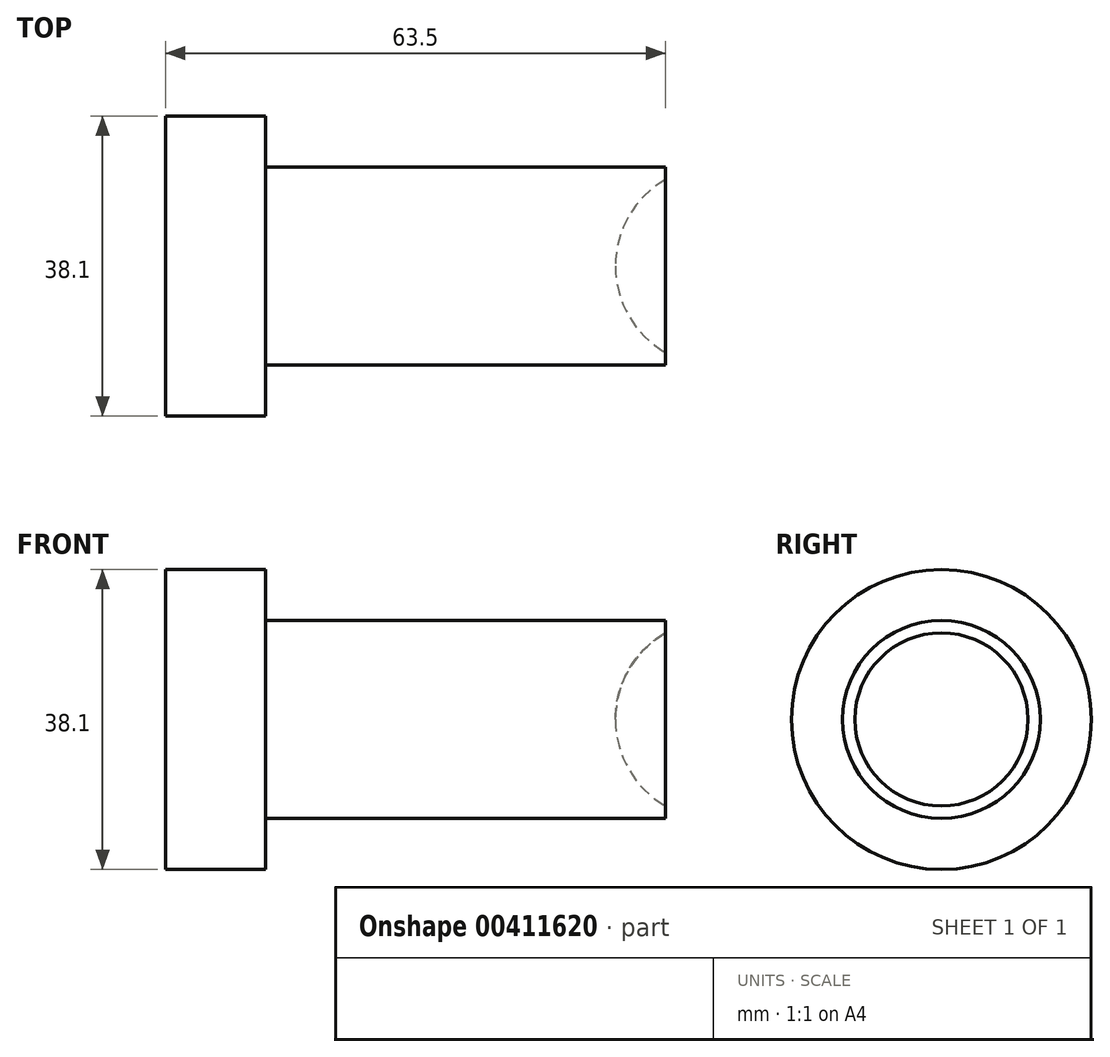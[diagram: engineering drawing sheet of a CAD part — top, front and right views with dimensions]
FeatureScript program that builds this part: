
annotation { "Feature Type Name" : "Feature", "Feature Type Description" : "" }
export const myFeature = defineFeature(function(context is Context, id is Id, definition is map)
    precondition{}
    {
        {
            var Q0;
            Q0=qCreatedBy(makeId("Right.planeOp"),FACE);
            var sketch = newSketch(context, id + "F0", { "sketchPlane" : qUnion([Q0])});
            skCircle(sketch, "E0", {"center": v(0, 0) * mm, "radius": 19.05 * mm});
            skSolve(sketch);
        }
        {
            var Q0;
            Q0 = qSketchRegion(id + "F0", true);
            extrude(context, id + "F1", {"entities" : qUnion([Q0]), "depth" : 12.7 * mm});
        }
        {
            var Q0;
            Q0=makeQuery(id+"F1.opExtrude","CAP_FACE",FACE,{"disambiguationData":[OSD([sQuery(id+"F0.wireOp",EDGE,"E0")])],"isStart":false});
            var sketch = newSketch(context, id + "F2", { "sketchPlane" : qUnion([Q0])});
            skCircle(sketch, "E1", {"center": v(0, 0) * mm, "radius": 12.57 * mm});
            skSolve(sketch);
        }
        {
            var Q0;
            Q0 = qSketchRegion(id + "F2", true);
            extrude(context, id + "F3", {"entities" : qUnion([Q0]), "operationType" : NewBodyOperationType.ADD, "depth" : 50.8 * mm});
        }
        {
            var Q0;
            Q0=qCreatedBy(makeId("Front.planeOp"),FACE);
            var sketch = newSketch(context, id + "F4", { "sketchPlane" : qUnion([Q0])});
            skArc(sketch, "E2", {"start": v(57.15, 0) * mm, "mid": v(69.85, -12.7) * mm, "end": v(82.55, 0) * mm});
            skLineSegment(sketch, "E3", {"start": v(57.15, 0) * mm, "end": v(82.55, 0) * mm});
            skSolve(sketch);
        }
        {
            var Q0;
            Q0 = qSketchRegion(id + "F4", true);
            var Q1;
            Q1=sQuery(id+"F4.wireOp",EDGE,"E3");
            revolve(context, id + "F5", {"operationType" : NewBodyOperationType.REMOVE, "entities" : qUnion([Q0]), "axis" : qUnion([Q1]), "revolveType" : RevolveType.FULL, "oppositeDirection" : true});
        }
    });
